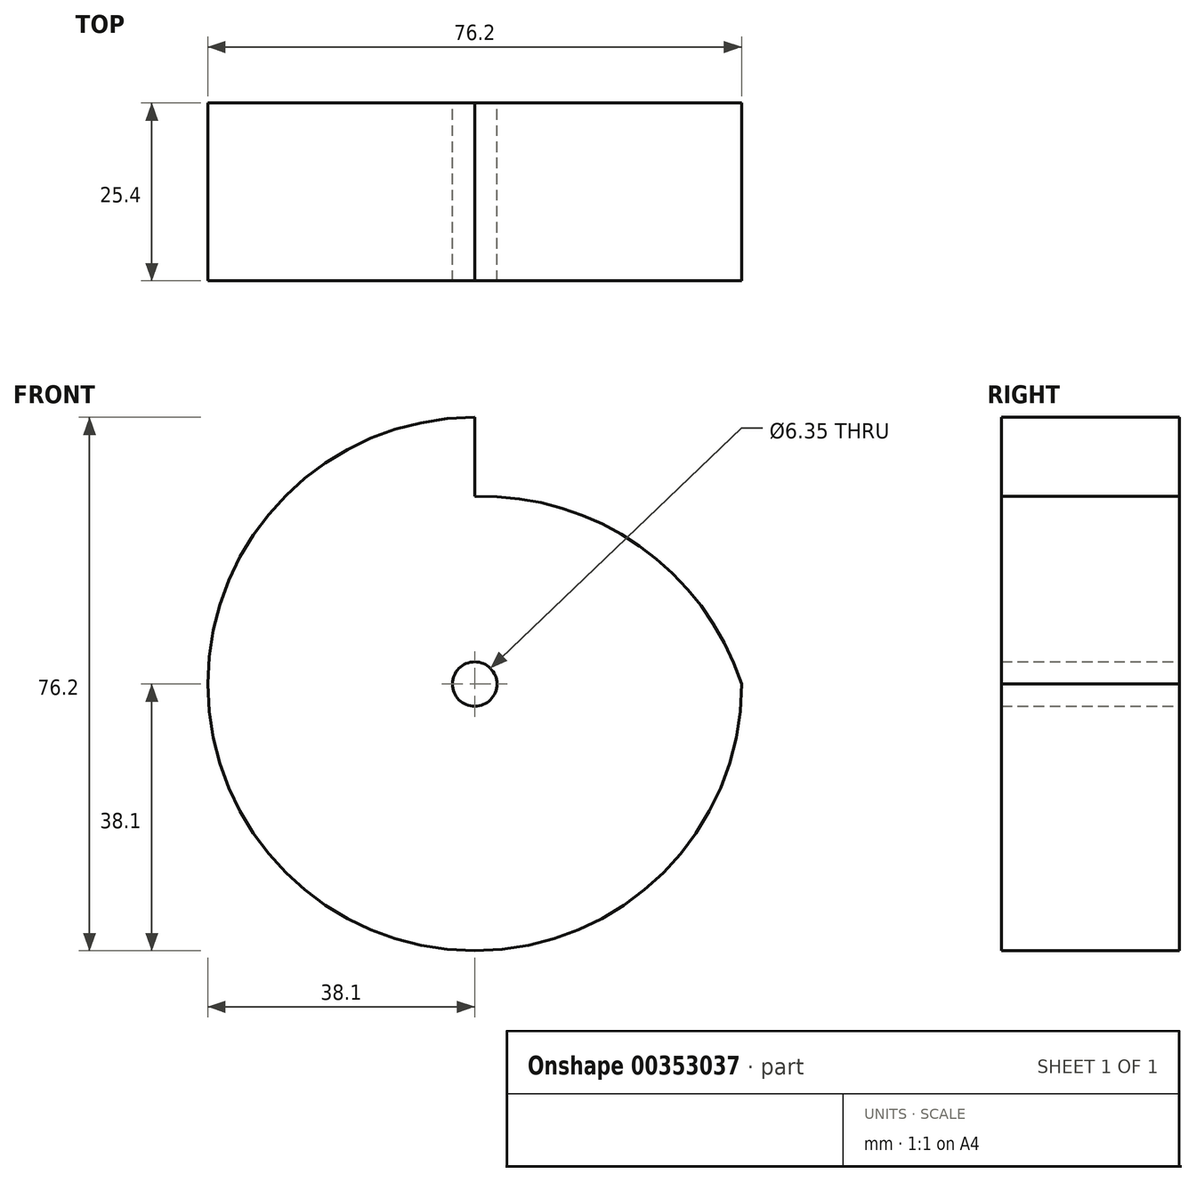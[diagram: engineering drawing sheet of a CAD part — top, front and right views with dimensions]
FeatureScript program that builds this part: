
annotation { "Feature Type Name" : "Feature", "Feature Type Description" : "" }
export const myFeature = defineFeature(function(context is Context, id is Id, definition is map)
    precondition{}
    {
        {
            var Q0;
            Q0=qCreatedBy(makeId("Front.planeOp"),FACE);
            var sketch = newSketch(context, id + "F0", { "sketchPlane" : qUnion([Q0])});
            skArc(sketch, "E0", {"start": v(0, 38.1) * mm, "mid": v(-26.94, -26.94) * mm, "end": v(38.1, 0) * mm});
            skCircle(sketch, "E1", {"center": v(0, 0) * mm, "radius": 3.18 * mm});
            skLineSegment(sketch, "E2", {"start": v(0, 38.1) * mm, "end": v(0, 26.8) * mm});
            skArc(sketch, "E3", {"start": v(38.1, 0) * mm, "mid": v(23.5, 19.73) * mm, "end": v(0, 26.8) * mm});
            skSolve(sketch);
        }
        {
            var Q0;
            Q0=makeQuery(id+"F0.imprint","IMPRINT",FACE,{"disambiguationData":[TD([[makeQuery(id+"F0.imprint","IMPRINT",EDGE,{"derivedFrom":sQuery(id+"F0.wireOp",EDGE,"E0")}),1.0]])]});
            extrude(context, id + "F1", {"entities" : qUnion([Q0]), "depth" : 25.4 * mm});
        }
    });
